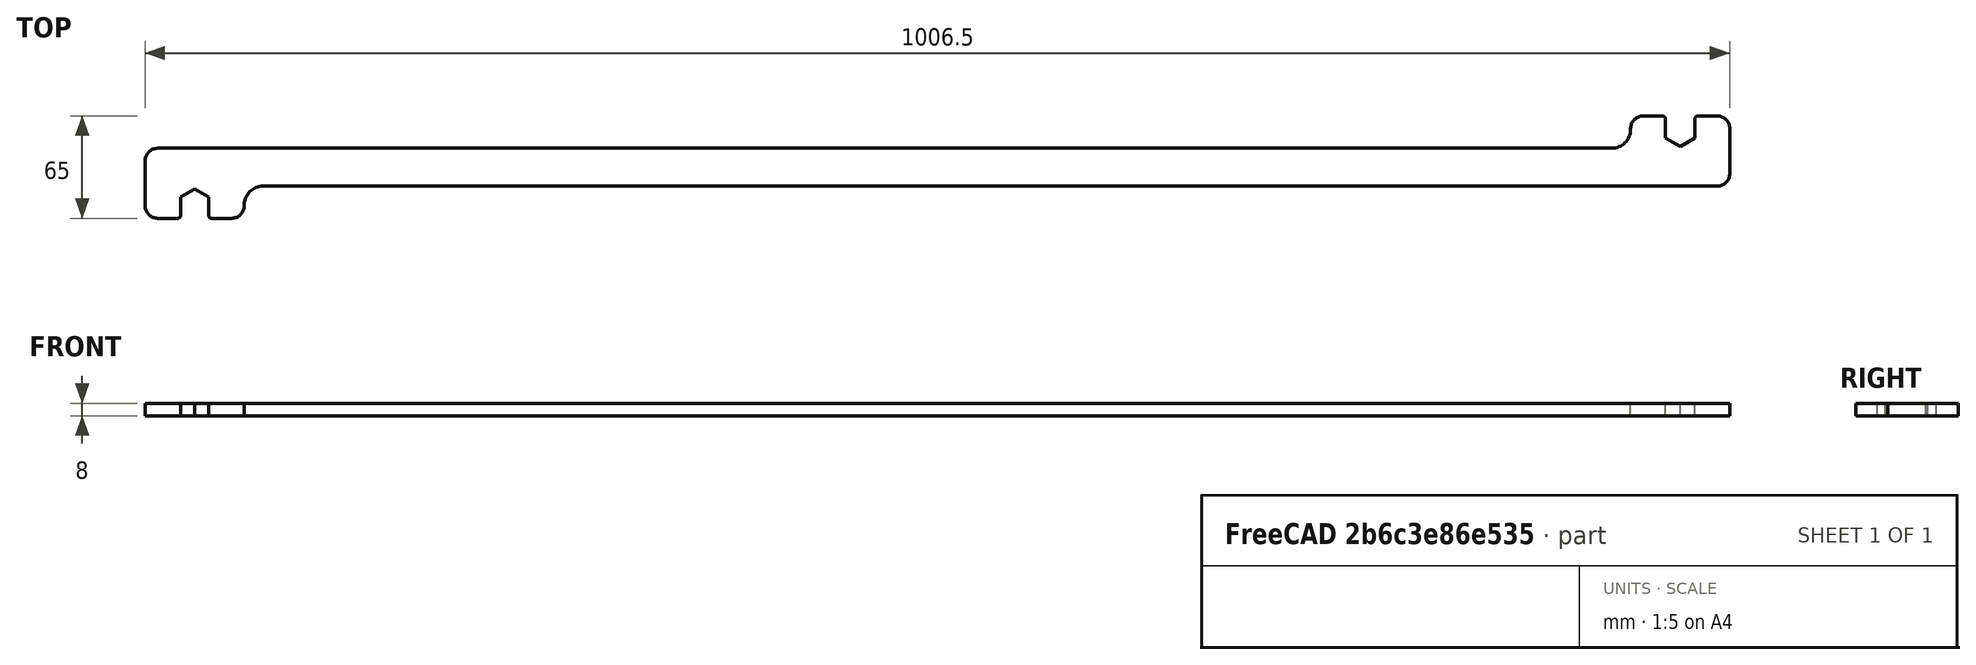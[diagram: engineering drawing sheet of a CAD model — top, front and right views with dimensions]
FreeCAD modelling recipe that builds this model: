
FCSTD DOCUMENT  (FreeCAD 0.19R24267 +99 (Git))
Label: V2 Long reach spanner FEA_CLEARED
License: All rights reserved
LicenseURL: http://en.wikipedia.org/wiki/All_rights_reserved
objects: Sketcher::SketchObject×1, PartDesign::Pad×1, PartDesign::Line×1, PartDesign::Body×1, Fem::FemSolverObjectPython×1, App::MaterialObjectPython×1, Fem::ConstraintFixed×1, Fem::ConstraintForce×1, Fem::FemMeshObjectPython×1, Fem::FemAnalysis×1
note: 5 computed .brp shape members not serialized (recipe doc carries the construction recipe); baked Part::Feature solids carry a one-line shape summary decoded from their .brp

FEATURE [Sketcher::SketchObject] Sketch
  FullyConstrained = true
  MapMode = 5
  Support = -> [XY_Plane]
  sketch-geometry (52):
    g0: LineSegment StartX=-428.25 StartY=12 StartZ=0 EndX=428.25 EndY=12 EndZ=0
    g1: LineSegment StartX=-428.25 StartY=-12 StartZ=0 EndX=428.25 EndY=-12 EndZ=0
    g2: LineSegment StartX=0 StartY=12 StartZ=0 EndX=0 EndY=-12 EndZ=0
    g3: LineSegment StartX=440.25 StartY=24 StartZ=0 EndX=440.25 EndY=24.5 EndZ=0
    g4: LineSegment StartX=448.25 StartY=32.5 StartZ=0 EndX=460.45 EndY=32.5 EndZ=0
    g5: LineSegment StartX=428.25 StartY=-12 StartZ=0 EndX=495.25 EndY=-12 EndZ=0
    g6: LineSegment StartX=503.25 StartY=24.5 StartZ=0 EndX=503.25 EndY=-4 EndZ=0
    g7: LineSegment StartX=-428.25 StartY=12 StartZ=0 EndX=-495.25 EndY=12 EndZ=0
    g8: LineSegment StartX=-503.25 StartY=4 StartZ=0 EndX=-503.25 EndY=-24.5 EndZ=0
    g9: LineSegment StartX=-495.25 StartY=-32.5 StartZ=0 EndX=-482.55 EndY=-32.5 EndZ=0
    g10: LineSegment StartX=-440.25 StartY=-24 StartZ=0 EndX=-440.25 EndY=-24.5 EndZ=0
    g11: ArcOfCircle CenterX=-495.25 CenterY=4 CenterZ=0 NormalX=0 NormalY=0 NormalZ=1 AngleXU=0 Radius=8 StartAngle=1.5708 EndAngle=3.14159
    g12: ArcOfCircle CenterX=-495.25 CenterY=-24.5 CenterZ=0 NormalX=0 NormalY=0 NormalZ=1 AngleXU=0 Radius=8 StartAngle=3.14159 EndAngle=4.71239
    g13: ArcOfCircle CenterX=-448.25 CenterY=-24.5 CenterZ=0 NormalX=0 NormalY=0 NormalZ=1 AngleXU=0 Radius=8 StartAngle=4.71239 EndAngle=6.28319
    g14: ArcOfCircle CenterX=-428.25 CenterY=-24 CenterZ=0 NormalX=0 NormalY=0 NormalZ=1 AngleXU=0 Radius=12 StartAngle=1.5708 EndAngle=3.14159
    g15: ArcOfCircle CenterX=428.25 CenterY=24 CenterZ=0 NormalX=0 NormalY=0 NormalZ=1 AngleXU=0 Radius=12 StartAngle=4.71239 EndAngle=6.28319
    g16: ArcOfCircle CenterX=448.25 CenterY=24.5 CenterZ=0 NormalX=0 NormalY=0 NormalZ=1 AngleXU=0 Radius=8 StartAngle=1.5708 EndAngle=3.14159
    g17: ArcOfCircle CenterX=495.25 CenterY=24.5 CenterZ=0 NormalX=0 NormalY=0 NormalZ=1 AngleXU=0 Radius=8 StartAngle=0 EndAngle=1.5708
    g18: ArcOfCircle CenterX=495.25 CenterY=-4 CenterZ=0 NormalX=0 NormalY=0 NormalZ=1 AngleXU=0 Radius=8 StartAngle=4.71239 EndAngle=6.28319
    g19: LineSegment StartX=-471.75 StartY=-32.5 StartZ=0 EndX=-471.75 EndY=-24 EndZ=0
    g20: LineSegment StartX=471.75 StartY=32.5 StartZ=0 EndX=471.75 EndY=24 EndZ=0
    g21: LineSegment StartX=471.75 StartY=24 StartZ=0 EndX=471.75 EndY=0 EndZ=0
    g22: LineSegment StartX=428.25 StartY=12 StartZ=0 EndX=503.25 EndY=12 EndZ=0
    g23: LineSegment StartX=-428.25 StartY=-12 StartZ=0 EndX=-503.25 EndY=-12 EndZ=0
    g24: LineSegment StartX=-471.75 StartY=-13.8386 StartZ=0 EndX=-471.75 EndY=-24 EndZ=0
    g25: LineSegment StartX=-471.75 StartY=-13.8386 StartZ=0 EndX=-480.55 EndY=-18.9193 EndZ=0
    g26: LineSegment StartX=-480.55 StartY=-18.9193 StartZ=0 EndX=-480.55 EndY=-29.0807 EndZ=0
    g27: LineSegment StartX=-480.55 StartY=-29.0807 StartZ=0 EndX=-471.75 EndY=-34.1614 EndZ=0
    g28: LineSegment StartX=-471.75 StartY=-34.1614 StartZ=0 EndX=-462.95 EndY=-29.0807 EndZ=0
    g29: LineSegment StartX=-462.95 StartY=-29.0807 StartZ=0 EndX=-462.95 EndY=-18.9193 EndZ=0
    g30: LineSegment StartX=-462.95 StartY=-18.9193 StartZ=0 EndX=-471.75 EndY=-13.8386 EndZ=0
    g31: Circle CenterX=-471.75 CenterY=-24 CenterZ=0 NormalX=0 NormalY=0 NormalZ=1 AngleXU=0 Radius=10.1614
    g32: LineSegment StartX=-480.55 StartY=-29.0807 StartZ=0 EndX=-480.55 EndY=-30.5 EndZ=0
    g33: LineSegment StartX=-462.95 StartY=-29.0807 StartZ=0 EndX=-462.95 EndY=-30.5 EndZ=0
    g34: LineSegment StartX=-460.95 StartY=-32.5 StartZ=0 EndX=-448.25 EndY=-32.5 EndZ=0
    g35: LineSegment StartX=-482.55 StartY=-32.5 StartZ=0 EndX=-460.95 EndY=-32.5 EndZ=0
    g36: ArcOfCircle CenterX=-482.55 CenterY=-30.5 CenterZ=0 NormalX=0 NormalY=0 NormalZ=1 AngleXU=0 Radius=2 StartAngle=4.71239 EndAngle=6.28319
    g37: ArcOfCircle CenterX=-460.95 CenterY=-30.5 CenterZ=0 NormalX=0 NormalY=0 NormalZ=1 AngleXU=0 Radius=2 StartAngle=3.14159 EndAngle=4.71239
    g38: LineSegment StartX=471.75 StartY=34.7387 StartZ=0 EndX=471.75 EndY=24 EndZ=0
    g39: LineSegment StartX=471.75 StartY=34.7387 StartZ=0 EndX=462.45 EndY=29.3694 EndZ=0
    g40: LineSegment StartX=462.45 StartY=29.3694 StartZ=0 EndX=462.45 EndY=18.6306 EndZ=0
    g41: LineSegment StartX=462.45 StartY=18.6306 StartZ=0 EndX=471.75 EndY=13.2613 EndZ=0
    g42: LineSegment StartX=471.75 StartY=13.2613 StartZ=0 EndX=481.05 EndY=18.6306 EndZ=0
    g43: LineSegment StartX=481.05 StartY=18.6306 StartZ=0 EndX=481.05 EndY=29.3694 EndZ=0
    g44: LineSegment StartX=481.05 StartY=29.3694 StartZ=0 EndX=471.75 EndY=34.7387 EndZ=0
    g45: Circle CenterX=471.75 CenterY=24 CenterZ=0 NormalX=0 NormalY=0 NormalZ=1 AngleXU=0 Radius=10.7387
    g46: LineSegment StartX=462.45 StartY=29.3694 StartZ=0 EndX=462.45 EndY=30.5 EndZ=0
    g47: LineSegment StartX=481.05 StartY=29.3694 StartZ=0 EndX=481.05 EndY=30.5 EndZ=0
    g48: LineSegment StartX=483.05 StartY=32.5 StartZ=0 EndX=495.25 EndY=32.5 EndZ=0
    g49: ArcOfCircle CenterX=460.45 CenterY=30.5 CenterZ=0 NormalX=0 NormalY=0 NormalZ=1 AngleXU=0 Radius=2 StartAngle=0 EndAngle=1.5708
    g50: ArcOfCircle CenterX=483.05 CenterY=30.5 CenterZ=0 NormalX=0 NormalY=0 NormalZ=1 AngleXU=0 Radius=2 StartAngle=1.5708 EndAngle=3.14159
    g51: LineSegment StartX=460.45 StartY=32.5 StartZ=0 EndX=483.05 EndY=32.5 EndZ=0
  constraints (124):
    c: Horizontal(g0)
    c: Symmetric(g2,g2,g-1)
    c: DistanceY(g2,g2) = 24  'Max width relative to head peaks'
    c: Vertical(g3)
    c: Horizontal(g4)
    c: Coincident(g5,g1)
    c: Horizontal(g5)
    c: Vertical(g6)
    c: Coincident(g7,g0)
    c: Horizontal(g7)
    c: Horizontal(g9)
    c: Vertical(g8)
    c: Tangent(g7,g11) = -1.5708
    c: Tangent(g8,g11) = -1.5708
    c: Tangent(g8,g12) = -1.5708
    c: Tangent(g9,g12) = -1.5708
    c: Tangent(g10,g13) = 1.5708
    c: Tangent(g10,g14) = -1.5708
    c: Tangent(g1,g14) = 1.5708
    c: Tangent(g3,g15) = -1.5708
    c: Tangent(g0,g15) = -1.5708
    c: Tangent(g4,g16) = 1.5708
    c: Tangent(g3,g16) = 1.5708
    c: Tangent(g6,g17) = 1.5708
    c: Tangent(g6,g18) = 1.5708
    c: Tangent(g5,g18) = -1.5708
    c: Radius(g15) = 12  'Shoulder radius'
    c: Radius(g16) = 8  'General radius'
    c: Equal(g16,g17)
    c: Equal(g17,g18)
    c: Equal(g18,g13)
    c: Equal(g13,g12)
    c: Equal(g12,g11)
    c: Vertical(g10)
    c: Equal(g14,g15)
    c: DistanceY(g-1,g48) = 32.5  'Centerline to box section inner wall - 6mm'
    c: Equal(g3,g10)
    c: Symmetric(g0,g1,g-1)
    c: Symmetric(g0,g1,g-1)
    c: Symmetric(g1,g1,g2)
    c: Vertical(g2)
    c: Symmetric(g9,g34,g19)
    c: Symmetric(g4,g48,g20)
    c: Equal(g20,g19)
    c: Coincident(g21,g20)
    c: PointOnObject(g21,g-1)
    c: Vertical(g21)
    c: DistanceY(g21,g21) = 24  'Bolt offset from centerline'
    c: Vertical(g20)
    c: DistanceX(g0,g6) = 75  '2x bolt interval - (2x 0.5 head max dia)'
    c: Coincident(g22,g0)
    c: PointOnObject(g22,g6)
    c: Horizontal(g22)
    c: Coincident(g23,g1)
    c: PointOnObject(g23,g8)
    c: Horizontal(g23)
    c: DistanceX(g1,g21) = 900  'Spanner useful length'
    c: Vertical(g24)
    c: Coincident(g25,g26)
    c: Coincident(g26,g27)
    c: Coincident(g27,g28)
    c: Coincident(g28,g29)
    c: Coincident(g29,g30)
    c: Coincident(g30,g25)
    c: Equal(g25, g26-g30) x5
    c: PointOnObject(g25,g31)
    c: PointOnObject(g26,g31)
    c: PointOnObject(g27,g31)
    c: PointOnObject(g28,g31)
    c: PointOnObject(g29,g31)
    c: PointOnObject(g30,g31)
    c: Coincident(g31,g24)
    c: Coincident(g30,g24)
    c: DistanceX(g25,g29) = 17.6
    c: Coincident(g19,g24)
    c: Coincident(g32,g26)
    c: Vertical(g32)
    c: Coincident(g33,g29)
    c: Vertical(g33)
    c: Tangent(g9,g34)
    c: PointOnObject(g19,g35)
    c: Tangent(g34,g13) = -1.5708
    c: Equal(g23,g22)
    c: Tangent(g32,g36) = 1.5708
    c: Tangent(g9,g36) = -1.5708
    c: Tangent(g33,g37) = -1.5708
    c: Tangent(g34,g37) = -1.5708
    c: Coincident(g9,g35)
    c: Coincident(g34,g35)
    c: Equal(g36,g37)
    c: Vertical(g38)
    c: Coincident(g39,g40)
    c: Coincident(g40,g41)
    c: Coincident(g41,g42)
    c: Coincident(g42,g43)
    c: Coincident(g43,g44)
    c: Coincident(g44,g39)
    c: Equal(g39, g40-g44) x5
    c: PointOnObject(g39,g45)
    c: PointOnObject(g40,g45)
    c: PointOnObject(g41,g45)
    c: PointOnObject(g42,g45)
    c: PointOnObject(g43,g45)
    c: PointOnObject(g44,g45)
    c: Coincident(g45,g38)
    c: DistanceX(g39,g43) = 18.6
    c: Coincident(g38,g39)
    c: Coincident(g38,g20)
    c: Coincident(g46,g40)
    c: Vertical(g46)
    c: Coincident(g47,g43)
    c: Vertical(g47)
    c: Tangent(g4,g48)
    c: Tangent(g46,g49) = -1.5708
    c: Tangent(g4,g49) = 1.5708
    c: Tangent(g47,g50) = 1.5708
    c: Tangent(g48,g50) = 1.5708
    c: Coincident(g51,g4)
    c: Coincident(g51,g48)
    c: Equal(g49,g50)
    c: Equal(g50,g36)
    c: Tangent(g48,g17) = 1.5708
    c: DistanceX(g3,g6) = 63
    c: Radius(g50) = 2
FEATURE [PartDesign::Pad] Pad
  Direction = (1,1,1)
  Length = 8
  Length2 = 100
  Profile = -> Sketch
  Type = 0
FEATURE [PartDesign::Line] DatumLine
  AttacherType = Attacher::AttachEngineLine
  Length = 20
  ResizeMode = 0
FEATURE [PartDesign::Body] Body
  Group = -> [Sketch,Pad,DatumLine]
  Origin = -> Origin
  Tip = -> Pad
FEATURE [Fem::FemSolverObjectPython] SolverCcxTools  # FEM object (typed FeaturePython)
  AnalysisType = 0
  BeamShellResultOutput3D = false
  EigenmodeHighLimit = 1000000
  EigenmodeLowLimit = 0
  EigenmodesCount = 10
  GeometricalNonlinearity = 0
  IterationsControlParameterCutb = 0.25,0.5,0.75,0.85,,,1.5,
  IterationsControlParameterIter = 4,8,9,200,10,400,,200,,
  IterationsControlParameterTimeUse = false
  IterationsThermoMechMaximum = 2000
  IterationsUserDefinedIncrementations = false
  IterationsUserDefinedTimeStepLength = false
  MaterialNonlinearity = 0
  MatrixSolverType = 0
  SplitInputWriter = false
  ThermoMechSteadyState = true
  TimeEnd = 1
  TimeInitialStep = 0.01
FEATURE [App::MaterialObjectPython] MaterialSolid  # material (typed FeaturePython)
  Category = 0
  Material = AuthorAndLicense=CalculiX-Steel,CardName=CalculiX-Steel,Density=7900 kg/m^3,Description=Standard steel material for CalculiX sample calculations,+7 more (map truncated)
FEATURE [Fem::ConstraintFixed] ConstraintFixed
  NormalDirection = (-0.5,-0.866025,0)
  Normals = (36) [(-0.5,-0.866025,0),(-0.5,-0.866025,0),(-0.5,-0.866025,0),(-0.5,-0.866025,0),(-0.5,-0.866025,0),(-0.5,-0.866025,0),(-0.5,-0.866025,0),+29 more]
  Points = (36) [(-462.95,-18.9193,8),(-467.35,-16.379,8),(-471.75,-13.8386,8),(-462.95,-18.9193,4),(-467.35,-16.379,4),(-471.75,-13.8386,4),(-462.95,-18.9193,0),+29 more]
  References = -> [Pad]
FEATURE [Fem::ConstraintForce] ConstraintForce
  DirectionVector = (-1.8e-15,1,0)
  Force = 100
  NormalDirection = (-1.8e-15,1,0)
  Points = (9) [(483.05,32.5,8),(489.15,32.5,8),(495.25,32.5,8),(483.05,32.5,4),(489.15,32.5,4),(495.25,32.5,4),(483.05,32.5,0),(489.15,32.5,0),(495.25,32.5,0)]
  References = -> [Pad]
FEATURE [Fem::FemMeshObjectPython] FEMMeshGmsh  # FEM object (typed FeaturePython)
  Algorithm2D = 0
  Algorithm3D = 0
  CharacteristicLengthMax = 2.5
  CharacteristicLengthMin = 0
  CoherenceMesh = true
  ElementDimension = 0
  ElementOrder = 1
  GeometryTolerance = 1e-06
  GroupsOfNodes = false
  HighOrderOptimize = false
  OptimizeNetgen = false
  OptimizeStd = true
  Part = -> Pad
  RecombineAll = false
  SecondOrderLinear = false
FEATURE [Fem::FemAnalysis] Analysis
  Group = -> [SolverCcxTools,MaterialSolid,ConstraintFixed,ConstraintForce,FEMMeshGmsh]
